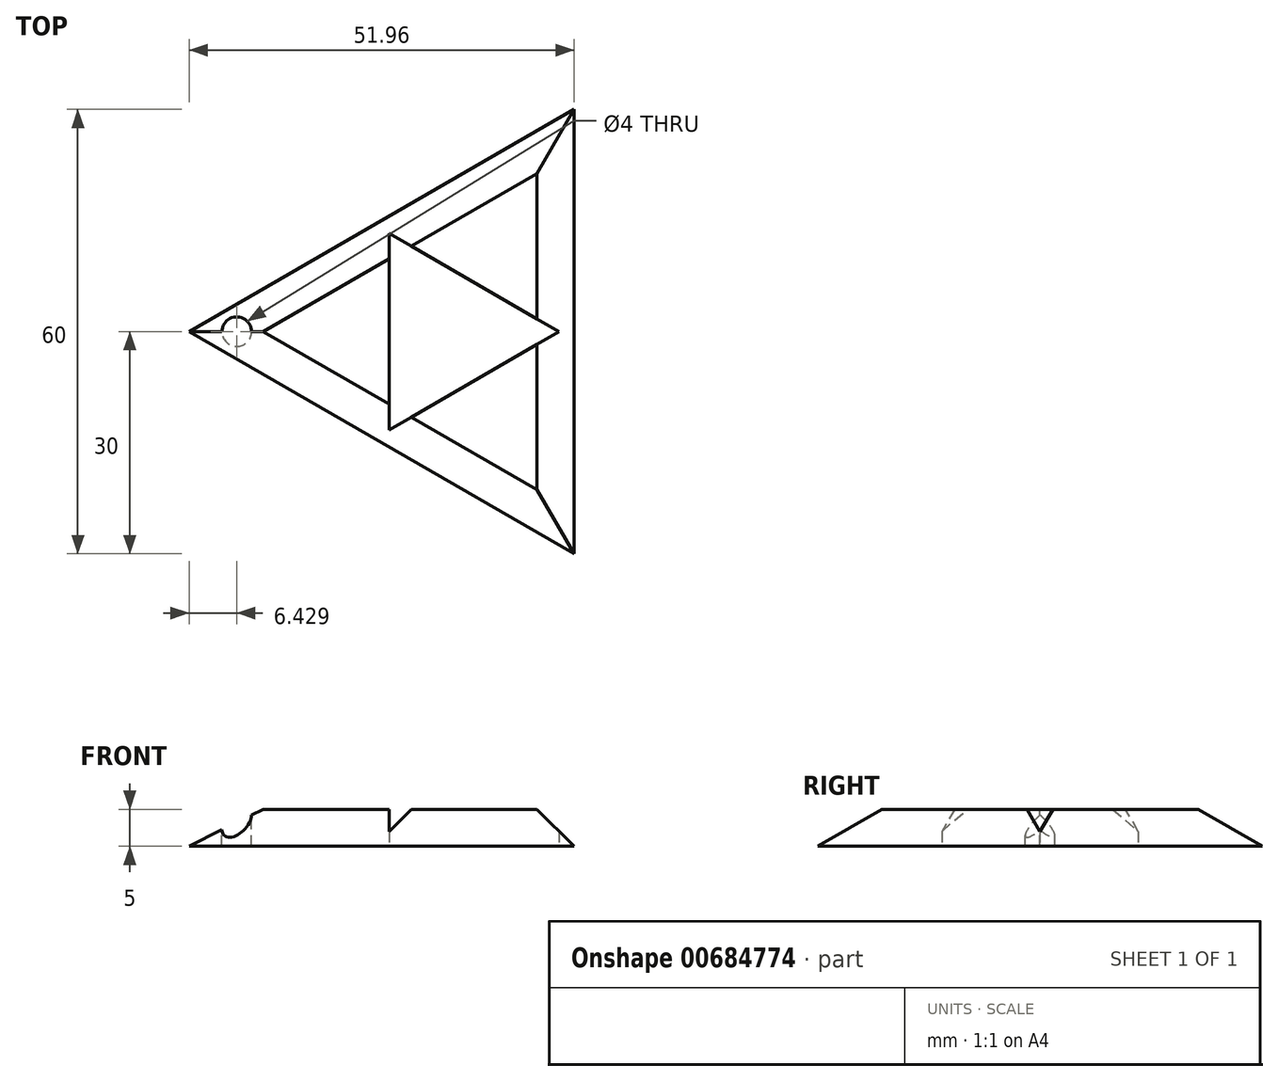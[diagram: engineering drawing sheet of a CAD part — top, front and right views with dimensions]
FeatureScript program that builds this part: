
annotation { "Feature Type Name" : "Feature", "Feature Type Description" : "" }
export const myFeature = defineFeature(function(context is Context, id is Id, definition is map)
    precondition{}
    {
        {
            var Q0;
            Q0=qCreatedBy(makeId("Top.planeOp"),FACE);
            var sketch = newSketch(context, id + "F0", { "sketchPlane" : qUnion([Q0])});
            skCircle(sketch, "E0.cCircle", {"center": v(0, 0) * mm, "radius": 17.32 * mm, "construction": true});
            skLineSegment(sketch, "E0.0", {"start": v(17.32, 30) * mm, "end": v(17.32, -30) * mm});
            skLineSegment(sketch, "E0.1", {"start": v(17.32, -30) * mm, "end": v(-34.64, 0) * mm});
            skLineSegment(sketch, "E0.2", {"start": v(-34.64, 0) * mm, "end": v(17.32, 30) * mm});
            skPoint(sketch, "E0.0.midPoint", {"position": v(17.32, 0) * mm});
            skPoint(sketch, "E1", {"position": v(-8.66, -15) * mm});
            skPoint(sketch, "E2", {"position": v(-8.66, 15) * mm});
            skLineSegment(sketch, "E3", {"start": v(-8.66, 15) * mm, "end": v(-7.66, 13.27) * mm, "construction": true});
            skLineSegment(sketch, "E4.1.0", {"start": v(-8.66, -15) * mm, "end": v(-7.66, -13.27) * mm, "construction": true});
            skLineSegment(sketch, "E4.2.0", {"start": v(17.32, 0) * mm, "end": v(15.32, 0) * mm, "construction": true});
            skLineSegment(sketch, "E5", {"start": v(-7.66, 13.27) * mm, "end": v(-7.66, -13.27) * mm});
            skLineSegment(sketch, "E6", {"start": v(-7.66, -13.27) * mm, "end": v(15.32, 0) * mm});
            skLineSegment(sketch, "E7", {"start": v(-7.66, 13.27) * mm, "end": v(15.32, 0) * mm});
            skSolve(sketch);
        }
        {
            var Q0;
            Q0=makeQuery(id+"F0.imprint","IMPRINT",FACE,{"disambiguationData":[TD([[makeQuery(id+"F0.imprint","IMPRINT",EDGE,{"derivedFrom":sQuery(id+"F0.wireOp",EDGE,"E0.0")}),-1.0]])]});
            extrude(context, id + "F1", {"entities" : qUnion([Q0]), "depth" : 5 * mm, "offsetDistance" : 25 * mm});
        }
        {
            var Q0;
            Q0=makeQuery(id+"F1.opExtrude","CAP_FACE",FACE,{"disambiguationData":[OSD([sQuery(id+"F0.wireOp",EDGE,"E0.0"),sQuery(id+"F0.wireOp",EDGE,"E0.1"),sQuery(id+"F0.wireOp",EDGE,"E0.2"),sQuery(id+"F0.wireOp",EDGE,"E5"),sQuery(id+"F0.wireOp",EDGE,"E6"),sQuery(id+"F0.wireOp",EDGE,"E7")])],"isStart":false});
            var sketch = newSketch(context, id + "F2", { "sketchPlane" : qUnion([Q0])});
            skCircle(sketch, "E8", {"center": v(-28.21, 0) * mm, "radius": 2 * mm});
            skPoint(sketch, "E8.centerSnap0", {"position": v(-7.66, 0) * mm});
            skSolve(sketch);
        }
        {
            var Q0;
            Q0=makeQuery(id+"F2.imprint","IMPRINT",FACE,{"disambiguationData":[TD([[makeQuery(id+"F2.imprint","IMPRINT",EDGE,{"derivedFrom":sQuery(id+"F2.wireOp",EDGE,"E8")}),1.0]])]});
            extrude(context, id + "F3", {"entities" : qUnion([Q0]), "operationType" : NewBodyOperationType.REMOVE, "oppositeDirection" : true, "depth" : 25 * mm, "offsetDistance" : 25 * mm});
        }
        {
            var Q0;
            Q0=makeQuery(id+"F1.opExtrude","CAP_EDGE",EDGE,{"disambiguationData":[OSD([sQuery(id+"F0.wireOp",EDGE,"E0.2")])],"isStart":false});
            var Q1;
            Q1=makeQuery(id+"F1.opExtrude","CAP_EDGE",EDGE,{"disambiguationData":[OSD([sQuery(id+"F0.wireOp",EDGE,"E0.0")])],"isStart":false});
            var Q2;
            Q2=makeQuery(id+"F1.opExtrude","CAP_EDGE",EDGE,{"disambiguationData":[OSD([sQuery(id+"F0.wireOp",EDGE,"E0.1")])],"isStart":false});
            chamfer(context, id + "F4", {"entities" : qUnion([Q0, Q1, Q2]), "width" : 5 * mm, "tangentPropagation" : true});
        }
    });
